# Revit family: Legrand Trimod UPS 10 80 kVA
name_source: partatom
category: Installations électriques
units: mm (PartAtom-declared; Revit-internal decimal feet)

## family parameters
Basée sur le plan de construction = Non
Conserver l'orientation des annotations = Non
Cote de connecteur circulaire = Utiliser le diamètre
Couper avec des vides une fois chargée = Non
Numéro OmniClass = 23.80.10.17.34
Partagée = Non
Repère de localisation dans la pièce = Non
Titre OmniClass = Static Uninterruptible Power Supplies
Toujours verticalement = Oui
Type d'élément = Normal

## types (1)
- Legrand Trimod UPS 10 80 kVA
    Altitude operation = Up to 1000 meters above sea level
    Architecture of the UPS = Modular Three-phase
    Bypass type = Static automatic and manual
    Communication Ports = 1 RS232 serial ports
    Control panel = Touch Screen, Status light
    Depth = 628 mm  [stored 2.06037 ft]
    Elévation par défaut = 0 mm  [stored 0 ft]
    Fabricant = LEGRAND
    General Conditions of Use = https://export.legrand.com
    Installation zone depth = 1728 mm
    Installation zone width = 814 mm  [stored 2.6706 ft]
    Max noise level = 58 to 62 dB at 1 meter
    Neutral = Neutral passing through
    Nominal load per module = 3 A
    Power factor = 0.99
    Typical installation = On the floor
    URL = https://ups.legrand.com
    Width = 414 mm  [stored 1.35827 ft]

note: [stored X ft] marks values corroborated as IEEE doubles in the binary element streams (Revit-internal decimal feet)
